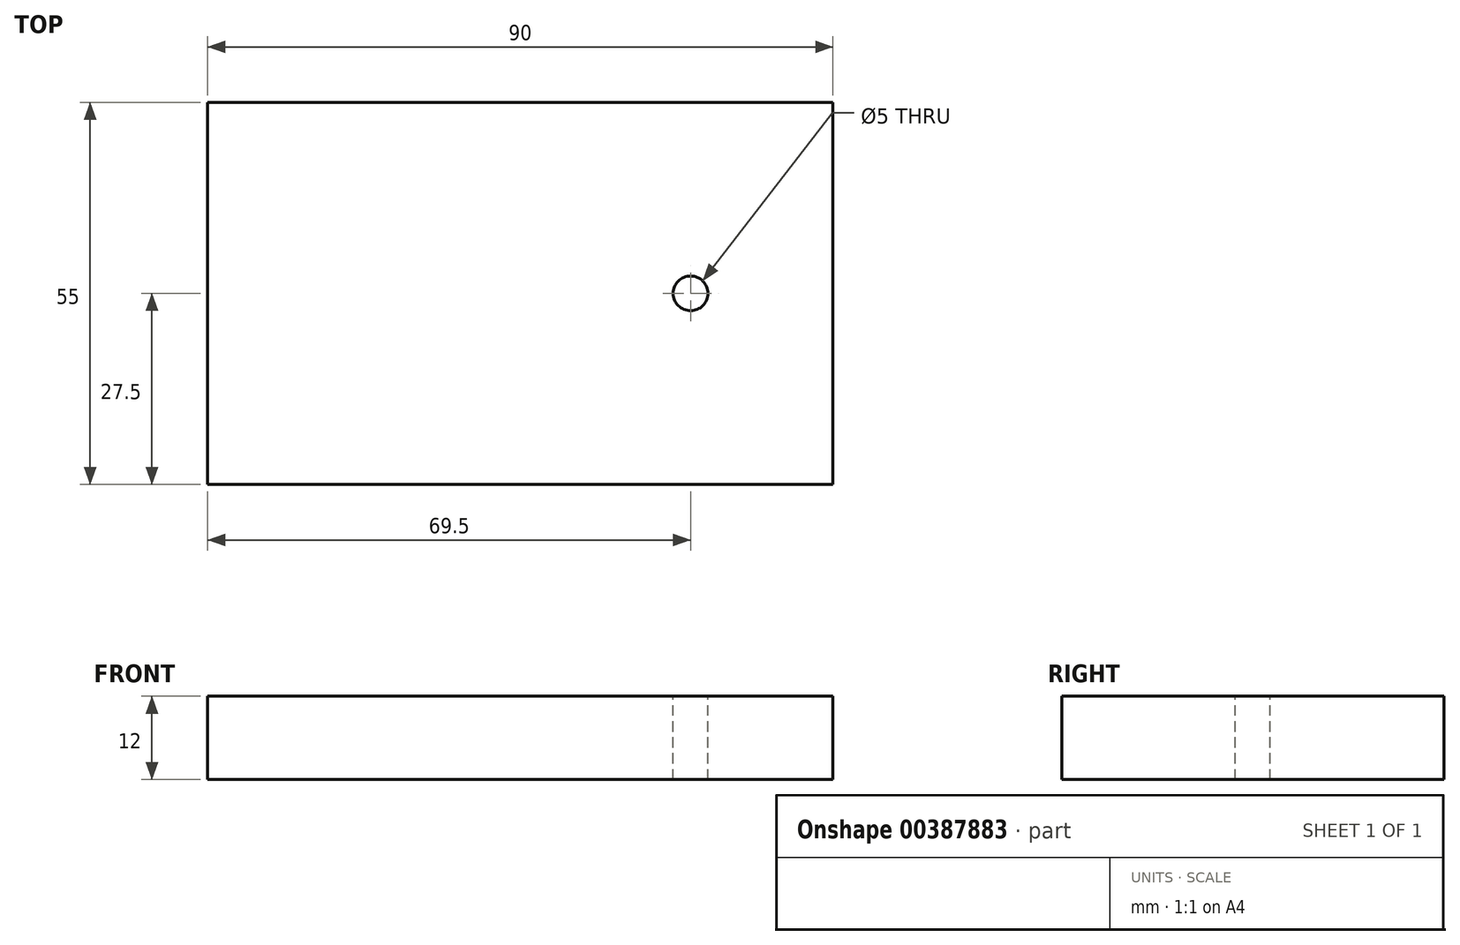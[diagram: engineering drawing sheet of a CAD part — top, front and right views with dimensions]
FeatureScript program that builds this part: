
annotation { "Feature Type Name" : "Feature", "Feature Type Description" : "" }
export const myFeature = defineFeature(function(context is Context, id is Id, definition is map)
    precondition{}
    {
        {
            var Q0;
            Q0=qCreatedBy(makeId("Top.planeOp"),FACE);
            var sketch = newSketch(context, id + "F0", { "sketchPlane" : qUnion([Q0])});
            skLineSegment(sketch, "E0.bottom", {"start": v(0, 0) * mm, "end": v(90, 0) * mm});
            skLineSegment(sketch, "E0.top", {"start": v(0, -55) * mm, "end": v(90, -55) * mm});
            skLineSegment(sketch, "E0.left", {"start": v(0, 0) * mm, "end": v(0, -55) * mm});
            skLineSegment(sketch, "E0.right", {"start": v(90, 0) * mm, "end": v(90, -55) * mm});
            skSolve(sketch);
        }
        {
            var Q0;
            Q0=makeQuery(id+"F0.imprint","IMPRINT",FACE,{"disambiguationData":[TD([[makeQuery(id+"F0.imprint","IMPRINT",EDGE,{"derivedFrom":sQuery(id+"F0.wireOp",EDGE,"E0.bottom")}),-1.0]])]});
            extrude(context, id + "F1", {"entities" : qUnion([Q0]), "depth" : 12 * mm});
        }
        {
            var Q0;
            Q0=makeQuery(id+"F1.opExtrude","CAP_FACE",FACE,{"disambiguationData":[OSD([sQuery(id+"F0.wireOp",EDGE,"E0.bottom"),sQuery(id+"F0.wireOp",EDGE,"E0.top"),sQuery(id+"F0.wireOp",EDGE,"E0.left"),sQuery(id+"F0.wireOp",EDGE,"E0.right")])],"isStart":false});
            var sketch = newSketch(context, id + "F2", { "sketchPlane" : qUnion([Q0])});
            skLineSegment(sketch, "E1", {"start": v(90, -27.5) * mm, "end": v(69.5, -27.5) * mm, "construction": true});
            skCircle(sketch, "E2", {"center": v(69.5, -27.5) * mm, "radius": 2.5 * mm});
            skSolve(sketch);
        }
        {
            var Q0;
            Q0=sQuery(id+"F2.wireOp",VERTEX,"E2.center");
            var Q1;
            Q1=makeQuery(id+"F1.opExtrude","SWEPT_BODY",BODY,{"disambiguationData":[OSD([sQuery(id+"F0.wireOp",EDGE,"E0.bottom"),sQuery(id+"F0.wireOp",EDGE,"E0.top"),sQuery(id+"F0.wireOp",EDGE,"E0.left"),sQuery(id+"F0.wireOp",EDGE,"E0.right")])]});
            hole(context, id + "F3", {"style" : HoleStyle.SIMPLE, "endStyle" : HoleEndStyle.BLIND, "holeDiameter" : 5 * mm, "holeDepth" : 12 * mm, "isTappedThrough" : true, "tappedDepth" : 12 * mm, "tapClearance" : 3, "locations" : qUnion([Q0]), "scope" : qUnion([Q1])});
        }
    });
